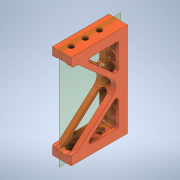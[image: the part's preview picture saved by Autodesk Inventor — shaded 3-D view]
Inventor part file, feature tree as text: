
AUTODESK INVENTOR PART (.ipt)
format: ipt  version: 2020 (Build 240168000, 168)  size: 579,584 bytes
history: native  units: in
note: dims shown in document units (in); Inventor stores cm internally (conversion verified against a paired STEP export)
features: extrude x12, sketch x10, projected_geometry x6, plane x5, fillet x4, chamfer x2
ambient origin geometry x8: Origin, YZ Plane, XZ Plane, XY Plane, X Axis, Y Axis, Z Axis, Center Point
bodies: Solid1 (feature_tree)
feature tree (39):
  extrude  "Extrusion1"  Depth=5.0in
  extrude  "Extrusion2"  Depth=0.5in
  fillet  "Fillet1"  Radius=0.5in
  extrude  "Extrusion3"  Depth=0.05in
  fillet  "Fillet2"  Radius=0.25in
  extrude  "Extrusion4"  Depth=0.5in
  plane  "Work Plane1"
  extrude  "Extrusion5"  Depth=2.5in
  extrude  "Extrusion6"  TaperAngle=0.0deg  [1 undecoded]
  plane  "Work Plane2"
  extrude  "Extrusion7"  Depth=0.4532in
  plane  "Work Plane3"
  extrude  "Extrusion8"  Depth=0.25in TaperAngle=0.0deg
  extrude  "Extrusion10"  Depth=0.5in
  plane  "Work Plane4"
  plane  "Work Plane5"
  extrude  "Extrusion11"  Depth=0.3937in
  chamfer  "Chamfer1"  [1 undecoded]
  extrude  "Extrusion12"  [1 undecoded]
  extrude  "Extrusion13"  Depth=0.4532in
  chamfer  "Chamfer2"  Distance=2.5in
  fillet  "Fillet3"  [1 undecoded]
  fillet  "Fillet4"  Radius=0.4532in
  sketch  "Sketch1"  dims[d0=1.0in d1=5.0in]
  sketch  "Sketch2"  dims[d2=3.0in d3=0.0in d4=0.5in d5=0.5in]
  sketch  "Sketch3"  dims[d6=0.0in d7=0.0in d8=0.05in d9=0.25in]
  sketch  "Sketch4"  dims[d10=1.0in d11=0.0in d12=0.5in d13=0.125in]
  sketch  "Sketch6"  dims[d14=0.2in d16=2.5in]
  sketch  "Sketch8"  dims[d17=4.3307in d19=0.5in d20=0.3937in d22=1.0in d24=0.0in d25=0.0in]
  sketch  "Sketch10"  dims[d26=-0.25in d27=0.4532in]
  sketch  "Sketch11"  dims[d28=3.5433in d30=0.5in d31=0.3937in d33=1.0in d35=0.25in d36=0.0in]
  sketch  "Sketch12"  dims[d37=1.0in d38=0.5in]
  projected_geometry  "Projected Loop1"
  projected_geometry  "Projected Loop2"
  projected_geometry  "Projected Loop3"
  sketch  "Sketch13"  dims[d39=0.2656in d40=1.1811in d42=0.75in d43=0.3937in d45=1.0in d47=0.0in d48=0.0in d49=-0.25in d50=0.4532in d51=2.5in d52=0.0in d53=-0.25in d54=0.4532in d55=2.5in d56=0.0in d59=0.375in d60=0.26in d61=0.0in d62=-0.5in d63=0.375in d64=0.375in d65=0.375in d66=0.4532in d67=0.0in d68=0.125in d69=0.125in d70=45.0deg d71=0.4532in d72=0.0in d73=0.975in d74=0.0in d75=0.125in d76=0.125in d77=45.0deg d78=0.125in d79=0.175in]
  projected_geometry  "Projected Loop4"
  projected_geometry  "Projected Loop5"
  projected_geometry  "Projected Loop6"
note: 4 required parameter values undecoded (feature->parameter linkage not recoverable at this tier; creation-order binding heuristic only, values carry confidence <= 0.55)
